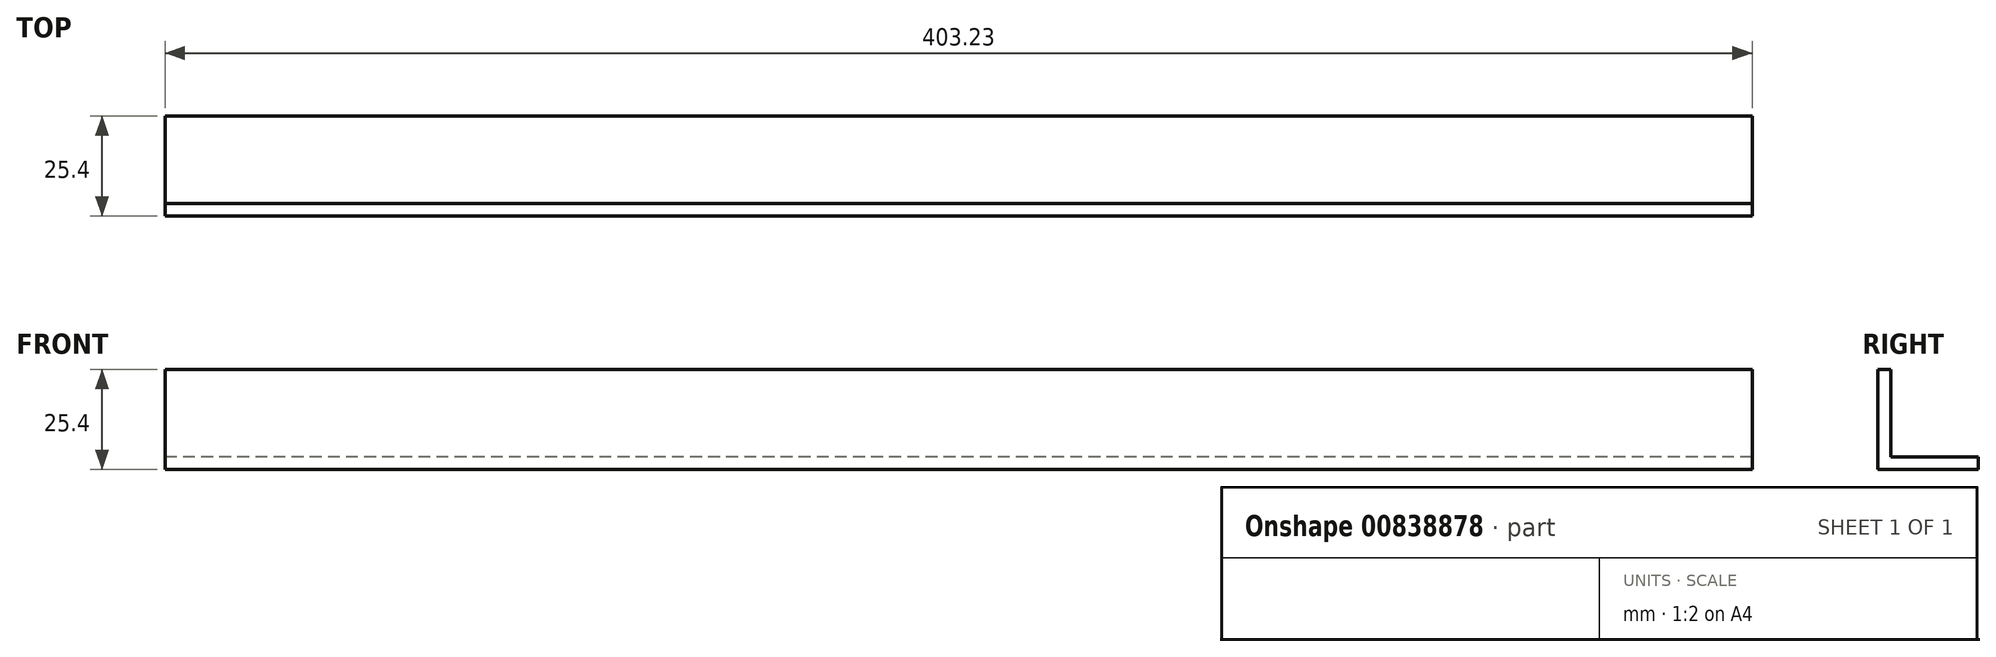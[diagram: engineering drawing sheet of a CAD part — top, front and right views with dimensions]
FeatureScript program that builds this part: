
annotation { "Feature Type Name" : "Feature", "Feature Type Description" : "" }
export const myFeature = defineFeature(function(context is Context, id is Id, definition is map)
    precondition{}
    {
        {
            var Q0;
            Q0=qCreatedBy(makeId("Right.planeOp"),FACE);
            var sketch = newSketch(context, id + "F0", { "sketchPlane" : qUnion([Q0])});
            skLineSegment(sketch, "E0", {"start": v(0, 0) * mm, "end": v(0, 25.4) * mm});
            skLineSegment(sketch, "E1", {"start": v(0, 25.4) * mm, "end": v(3.17, 25.4) * mm});
            skLineSegment(sketch, "E2", {"start": v(3.17, 25.4) * mm, "end": v(3.18, 3.17) * mm});
            skLineSegment(sketch, "E3", {"start": v(3.18, 3.17) * mm, "end": v(25.4, 3.18) * mm});
            skLineSegment(sketch, "E4", {"start": v(25.4, 3.18) * mm, "end": v(25.4, 0) * mm});
            skLineSegment(sketch, "E5", {"start": v(25.4, 0) * mm, "end": v(0, 0) * mm});
            skSolve(sketch);
        }
        {
            var Q0;
            Q0=makeQuery(id+"F0.imprint","IMPRINT",FACE,{"disambiguationData":[TD([[makeQuery(id+"F0.imprint","IMPRINT",EDGE,{"derivedFrom":sQuery(id+"F0.wireOp",EDGE,"E0")}),-1.0]])]});
            extrude(context, id + "F1", {"entities" : qUnion([Q0]), "depth" : 403.22 * mm, "offsetDistance" : 25.4 * mm});
        }
    });
